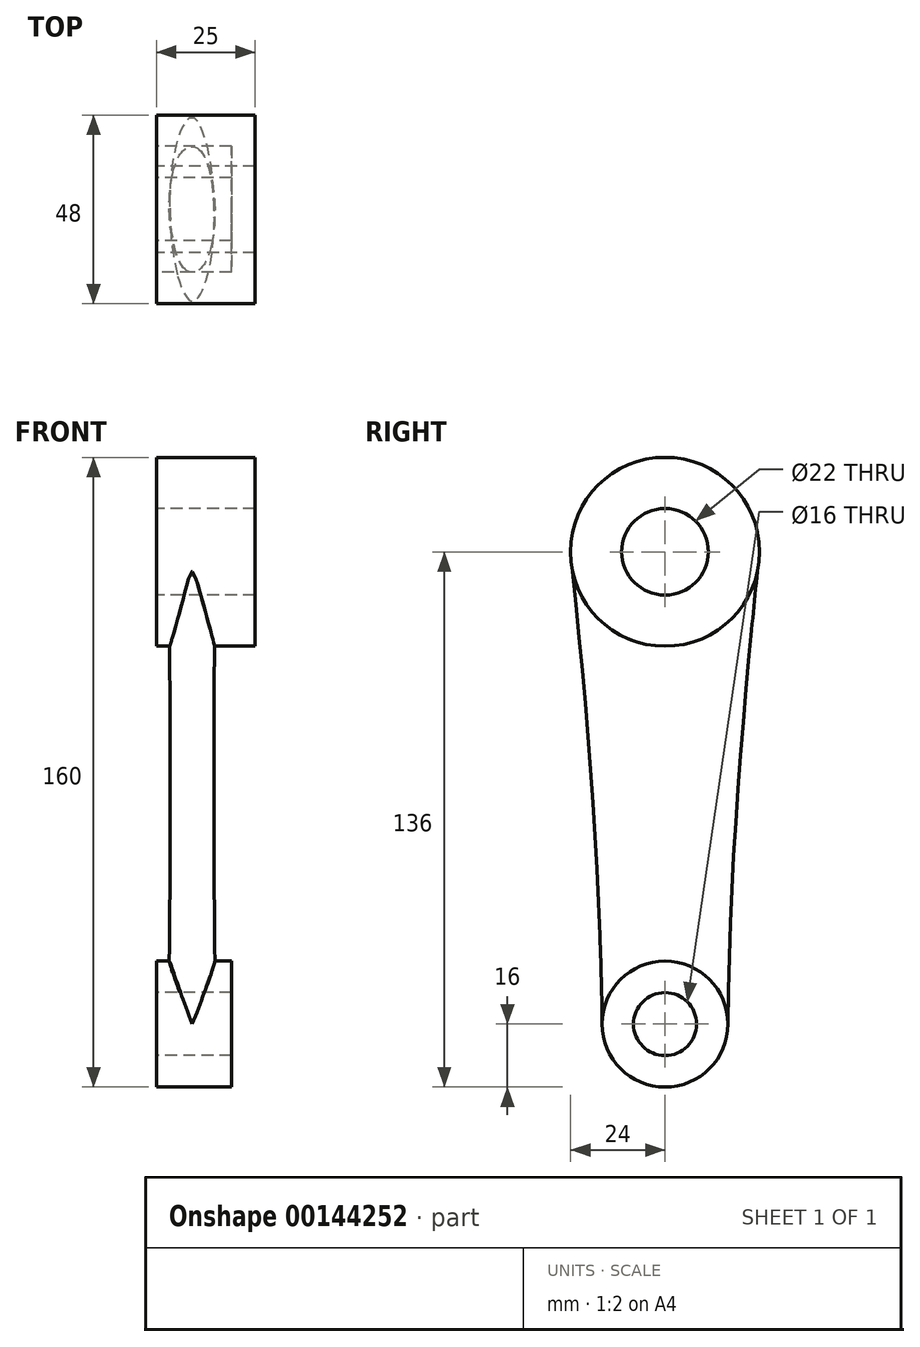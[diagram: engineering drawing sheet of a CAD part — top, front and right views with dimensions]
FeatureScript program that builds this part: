
annotation { "Feature Type Name" : "Feature", "Feature Type Description" : "" }
export const myFeature = defineFeature(function(context is Context, id is Id, definition is map)
    precondition{}
    {
        {
            var Q0;
            Q0=qCreatedBy(makeId("Right.planeOp"),FACE);
            var sketch = newSketch(context, id + "F0", { "sketchPlane" : qUnion([Q0])});
            skCircle(sketch, "E0", {"center": v(0, 0) * mm, "radius": 16 * mm});
            skCircle(sketch, "E1", {"center": v(0, 0) * mm, "radius": 8 * mm});
            skCircle(sketch, "E2", {"center": v(0, 120) * mm, "radius": 24 * mm});
            skCircle(sketch, "E3", {"center": v(0, 120) * mm, "radius": 11 * mm});
            skSolve(sketch);
        }
        {
            var Q0;
            Q0=makeQuery(id+"F0.imprint","IMPRINT",FACE,{"disambiguationData":[TD([[makeQuery(id+"F0.imprint","IMPRINT",EDGE,{"derivedFrom":sQuery(id+"F0.wireOp",EDGE,"E2")}),1.0]])]});
            var Q1;
            Q1=makeQuery(id+"F0.imprint","IMPRINT",FACE,{"disambiguationData":[TD([[makeQuery(id+"F0.imprint","IMPRINT",EDGE,{"derivedFrom":sQuery(id+"F0.wireOp",EDGE,"E3")}),1.0]])]});
            extrude(context, id + "F1", {"entities" : qUnion([Q0, Q1]), "depth" : 25 * mm});
        }
        {
            var Q0;
            Q0=makeQuery(id+"F0.imprint","IMPRINT",FACE,{"disambiguationData":[TD([[makeQuery(id+"F0.imprint","IMPRINT",EDGE,{"derivedFrom":sQuery(id+"F0.wireOp",EDGE,"E0")}),1.0]])]});
            var Q1;
            Q1=makeQuery(id+"F0.imprint","IMPRINT",FACE,{"disambiguationData":[TD([[makeQuery(id+"F0.imprint","IMPRINT",EDGE,{"derivedFrom":sQuery(id+"F0.wireOp",EDGE,"E1")}),1.0]])]});
            extrude(context, id + "F2", {"entities" : qUnion([Q0, Q1]), "depth" : 19 * mm});
        }
        {
            var Q0;
            Q0=qCreatedBy(makeId("Top.planeOp"),FACE);
            var sketch = newSketch(context, id + "F3", { "sketchPlane" : qUnion([Q0])});
            skLineSegment(sketch, "E4", {"start": v(0, 16) * mm, "end": v(18.78, 16) * mm, "construction": true});
            skEllipse(sketch, "E5", {"center": v(9, 0) * mm, "majorRadius": 16 * mm, "minorRadius": 6 * mm, "majorAxis": v(0, -1)});
            skPoint(sketch, "E6", {"position": v(3, 0) * mm});
            skSolve(sketch);
        }
        {
            var Q0;
            Q0=qCreatedBy(makeId("Top.planeOp"),FACE);
            var Q1;
            Q1=sQuery(id+"F0.wireOp",VERTEX,"E2.center");
            cPlane(context, id + "F4", {"entities" : qUnion([Q0, Q1]), "cplaneType" : CPlaneType.PLANE_POINT, "offset" : 25 * mm, "width" : 150 * mm, "height" : 150 * mm});
        }
        {
            var Q0;
            Q0=qCreatedBy(id+"F4.planeOp",FACE);
            var sketch = newSketch(context, id + "F5", { "sketchPlane" : qUnion([Q0])});
            skEllipse(sketch, "E7", {"center": v(9, 0) * mm, "majorRadius": 24 * mm, "minorRadius": 6 * mm, "majorAxis": v(0, -1)});
            skLineSegment(sketch, "E8", {"start": v(0, 24) * mm, "end": v(24.8, 24) * mm, "construction": true});
            skPoint(sketch, "E9", {"position": v(3, 0) * mm});
            skSolve(sketch);
        }
        {
            var Q0;
            Q0 = qSketchRegion(id + "F3", true);
            var Q1;
            Q1 = qSketchRegion(id + "F5", true);
            loft(context, id + "F6", {"operationType" : NewBodyOperationType.ADD, "sheetProfilesArray" : [{ "sheetProfileEntities" : qUnion([Q0]) }, { "sheetProfileEntities" : qUnion([Q1]) }]});
        }
        {
            var Q0;
            Q0=makeQuery(id+"F0.imprint","IMPRINT",FACE,{"disambiguationData":[TD([[makeQuery(id+"F0.imprint","IMPRINT",EDGE,{"derivedFrom":sQuery(id+"F0.wireOp",EDGE,"E3")}),1.0]])]});
            extrude(context, id + "F7", {"entities" : qUnion([Q0]), "operationType" : NewBodyOperationType.REMOVE, "endBound" : BoundingType.THROUGH_ALL, "depth" : 25 * mm});
        }
        {
            var Q0;
            Q0=makeQuery(id+"F0.imprint","IMPRINT",FACE,{"disambiguationData":[TD([[makeQuery(id+"F0.imprint","IMPRINT",EDGE,{"derivedFrom":sQuery(id+"F0.wireOp",EDGE,"E1")}),1.0]])]});
            var Q1;
            Q1=sQuery(id+"F0.wireOp",EDGE,"E1");
            extrude(context, id + "F8", {"entities" : qUnion([Q0]), "operationType" : NewBodyOperationType.REMOVE, "surfaceEntities" : qUnion([Q1]), "endBound" : BoundingType.THROUGH_ALL, "oppositeDirection" : true, "depth" : 25 * mm});
        }
        {
            var Q0;
            Q0=makeQuery(id+"F0.imprint","IMPRINT",FACE,{"disambiguationData":[TD([[makeQuery(id+"F0.imprint","IMPRINT",EDGE,{"derivedFrom":sQuery(id+"F0.wireOp",EDGE,"E1")}),1.0]])]});
            extrude(context, id + "F9", {"entities" : qUnion([Q0]), "operationType" : NewBodyOperationType.REMOVE, "endBound" : BoundingType.THROUGH_ALL, "depth" : 25 * mm});
        }
    });
